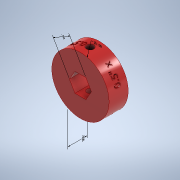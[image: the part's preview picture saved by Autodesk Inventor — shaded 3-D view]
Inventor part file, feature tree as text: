
AUTODESK INVENTOR PART (.ipt)
format: ipt  version: 2022.2 (Build 262287000, 287)  size: 1,085,440 bytes
history: native  units: in
note: dims shown in document units (in); Inventor stores cm internally (conversion verified against a paired STEP export)
features: sketch x5, other x4, extrude x3, plane x2, emboss x1, hole x1
ambient origin geometry x8: Origin, YZ Plane, XZ Plane, XY Plane, X Axis, Y Axis, Z Axis, Center Point
bodies: Solid1 (feature_tree)
feature tree (16):
  other  "Annotations"
  extrude  "Extrusion1"  Depth=1.5in
  plane  "Work Plane1"
  emboss  "Emboss1"
  hole  "Hole1"  [1 undecoded]
  extrude  "Extrusion2"  Depth=0.25in
  plane  "Work Plane2"
  extrude  "Extrusion3"  Depth=0.25in
  sketch  "Sketch1"  dims[d0=0.5in d2=1.5in]
  sketch  "Sketch2"  dims[d3=0.4613in d4=0.5in d5=0.0in]
  sketch  "Sketch3"  dims[d17=1.0in d18=0.25in]
  sketch  "Sketch4"  dims[d19=0.1in d20=0.0in]
  sketch  "Sketch5"  dims[d21=0.17in d22=0.75in d23=0.5in d24=0.093in d25=0.5635in d26=0.25in d27=0.0in d28=0.25in d29=0.25in d30=0.191in d31=0.2186in d32=0.0in d33=0.27in d34=0.073in d35=0.0in d10=0.5245in d11=1.5in d12=0.1538in d13=0.5in d14=0.1112in d15=0.3058in d16=0.5in]
  other  "Diameter Dimension 1"
  other  "Linear Dimension 1"
  other  "Linear Dimension 2"
note: 1 required parameter value undecoded (feature->parameter linkage not recoverable at this tier; creation-order binding heuristic only, values carry confidence <= 0.55)
